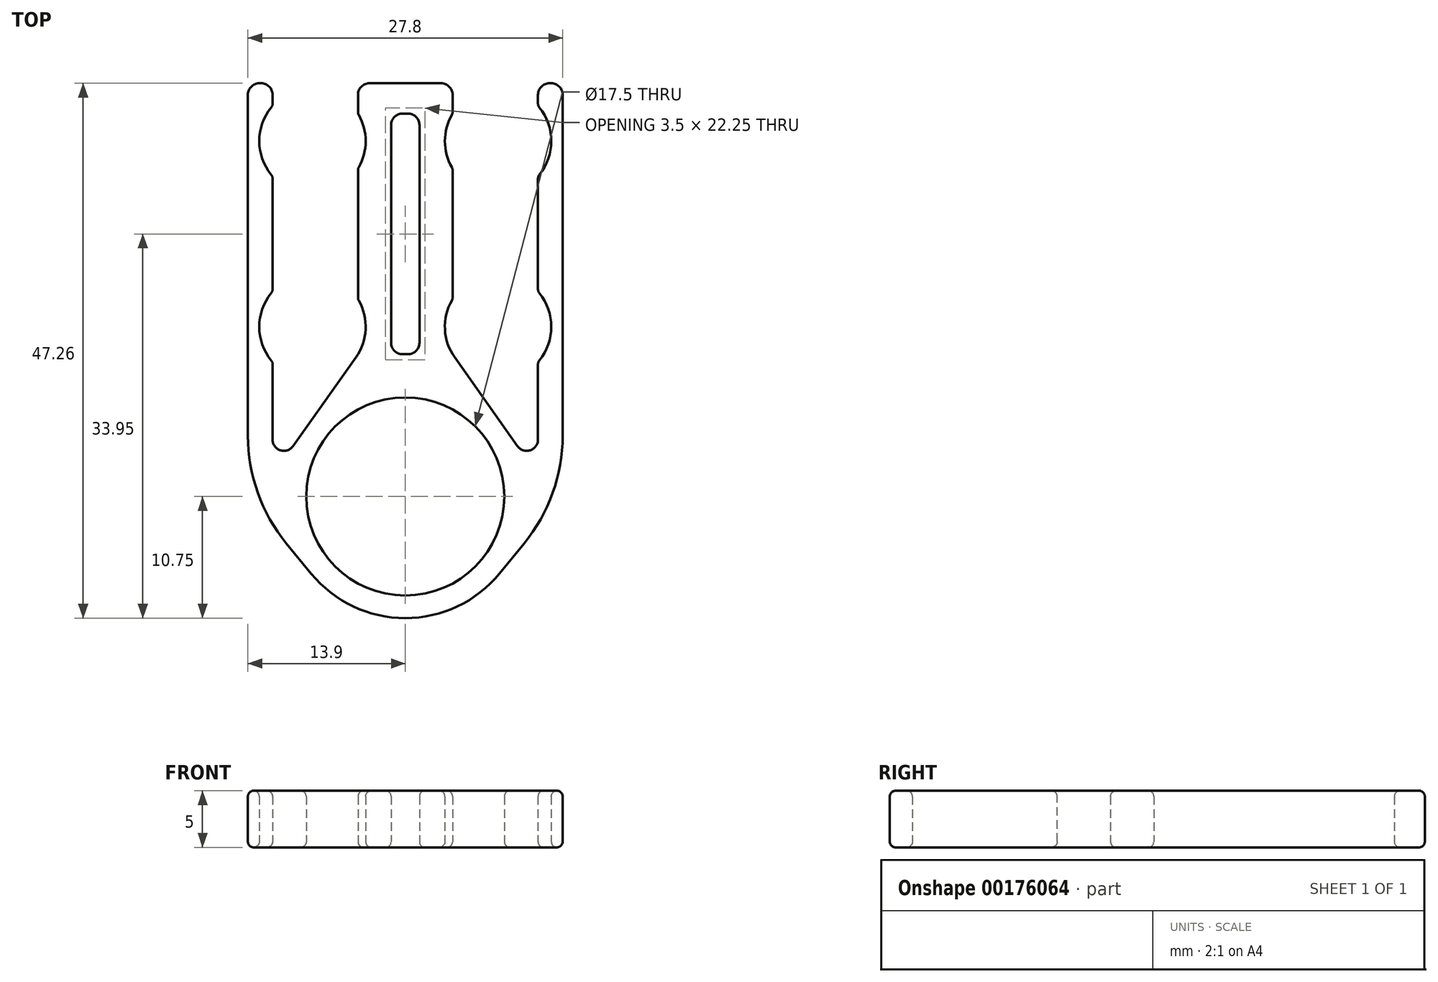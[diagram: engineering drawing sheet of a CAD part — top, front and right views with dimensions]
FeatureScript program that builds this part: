
annotation { "Feature Type Name" : "Feature", "Feature Type Description" : "" }
export const myFeature = defineFeature(function(context is Context, id is Id, definition is map)
    precondition{}
    {
        {
            var Q0;
            Q0=qCreatedBy(makeId("Top.planeOp"),FACE);
            var sketch = newSketch(context, id + "F0", { "sketchPlane" : qUnion([Q0])});
            skArc(sketch, "E0", {"start": v(-3.53, 3.1) * mm, "mid": v(-4.7, 0) * mm, "end": v(-3.53, -3.1) * mm});
            skArc(sketch, "E1.0.1.0", {"start": v(-3.53, 19.5) * mm, "mid": v(-4.7, 16.4) * mm, "end": v(-3.53, 13.3) * mm});
            skArc(sketch, "E1.1.0.0", {"start": v(19.92, -3.1) * mm, "mid": v(21.1, 0) * mm, "end": v(19.92, 3.1) * mm});
            skArc(sketch, "E1.1.1.0", {"start": v(19.92, 13.3) * mm, "mid": v(21.1, 16.4) * mm, "end": v(19.92, 19.5) * mm});
            skLineSegment(sketch, "E1.direction1", {"start": v(0, 0) * mm, "end": v(16.4, 0) * mm, "construction": true});
            skLineSegment(sketch, "E1.direction2", {"start": v(0, 0) * mm, "end": v(0, 16.4) * mm, "construction": true});
            skLineSegment(sketch, "E2", {"start": v(0, 16.4) * mm, "end": v(-4.7, 16.4) * mm, "construction": true});
            skLineSegment(sketch, "E3", {"start": v(16.4, 16.4) * mm, "end": v(21.1, 16.4) * mm, "construction": true});
            skLineSegment(sketch, "E4", {"start": v(16.4, 16.4) * mm, "end": v(11.7, 16.4) * mm, "construction": true});
            skLineSegment(sketch, "E5", {"start": v(0, 16.4) * mm, "end": v(4.7, 16.4) * mm, "construction": true});
            skPoint(sketch, "E6.startSnap0", {"position": v(-2.35, 16.4) * mm});
            skLineSegment(sketch, "E7", {"start": v(8.2, 0) * mm, "end": v(8.2, 16.4) * mm, "construction": true});
            skLineSegment(sketch, "E8", {"start": v(-4.7, 16.4) * mm, "end": v(-2.35, 16.4) * mm, "construction": true});
            skLineSegment(sketch, "E9", {"start": v(-3.53, 13.3) * mm, "end": v(-3.53, 3.1) * mm});
            skPoint(sketch, "E9.startSnap0", {"position": v(-3.53, 16.4) * mm});
            skLineSegment(sketch, "E10.MirrorCS", {"start": v(3.53, 13.3) * mm, "end": v(3.53, 3.1) * mm, "construction": true});
            skLineSegment(sketch, "E11.MirrorCS", {"start": v(19.92, 13.3) * mm, "end": v(19.92, 3.1) * mm});
            skLineSegment(sketch, "E12", {"start": v(-5.7, 21.5) * mm, "end": v(-5.7, 0) * mm});
            skLineSegment(sketch, "E13.0", {"start": v(4.03, 13.97) * mm, "end": v(4.03, 2.43) * mm});
            skLineSegment(sketch, "E14.MirrorCS", {"start": v(12.37, 13.97) * mm, "end": v(12.37, 2.43) * mm});
            skLineSegment(sketch, "E15", {"start": v(-5.7, 0) * mm, "end": v(-5.7, -15) * mm});
            skLineSegment(sketch, "E16", {"start": v(-3.53, -3.1) * mm, "end": v(-3.53, -13.1) * mm});
            skLineSegment(sketch, "E17", {"start": v(-3.53, -13.1) * mm, "end": v(3.84, -2.72) * mm});
            skCircle(sketch, "E18", {"center": v(8.2, -15) * mm, "radius": 8.75 * mm});
            skArc(sketch, "E19.0", {"start": v(-0.11, -21.81) * mm, "mid": v(8.2, -25.75) * mm, "end": v(16.51, -21.81) * mm});
            skLineSegment(sketch, "E20", {"start": v(-5.7, -15) * mm, "end": v(-0.11, -21.81) * mm});
            skLineSegment(sketch, "E21", {"start": v(-3.53, 19.5) * mm, "end": v(-3.53, 21.5) * mm});
            skLineSegment(sketch, "E22", {"start": v(-3.53, 21.5) * mm, "end": v(-5.7, 21.5) * mm});
            skPoint(sketch, "E23.orphan", {"position": v(-5.7, 16.4) * mm});
            skLineSegment(sketch, "E24", {"start": v(8.2, 16.4) * mm, "end": v(8.2, 21.5) * mm, "construction": true});
            skLineSegment(sketch, "E25", {"start": v(8.2, 21.5) * mm, "end": v(4.03, 21.5) * mm});
            skLineSegment(sketch, "E26", {"start": v(4.03, 21.5) * mm, "end": v(4.03, 18.83) * mm});
            skLineSegment(sketch, "E27.MirrorCS", {"start": v(8.2, 21.5) * mm, "end": v(12.37, 21.5) * mm});
            skLineSegment(sketch, "E28.MirrorCS", {"start": v(12.37, 21.5) * mm, "end": v(12.37, 18.83) * mm});
            skLineSegment(sketch, "E29.MirrorCS", {"start": v(19.92, 19.5) * mm, "end": v(19.92, 21.5) * mm});
            skLineSegment(sketch, "E30.MirrorCS", {"start": v(19.92, 21.5) * mm, "end": v(22.1, 21.5) * mm});
            skLineSegment(sketch, "E31.MirrorCS", {"start": v(22.1, 21.5) * mm, "end": v(22.1, 0) * mm});
            skLineSegment(sketch, "E32.MirrorCS", {"start": v(22.1, 0) * mm, "end": v(22.1, -15) * mm});
            skLineSegment(sketch, "E33.MirrorCS", {"start": v(22.1, -15) * mm, "end": v(16.51, -21.81) * mm});
            skLineSegment(sketch, "E34.MirrorCS", {"start": v(19.92, -13.1) * mm, "end": v(12.56, -2.72) * mm});
            skLineSegment(sketch, "E35.MirrorCS", {"start": v(19.92, -3.1) * mm, "end": v(19.92, -13.1) * mm});
            skArc(sketch, "E36.trimOffspring", {"start": v(17.7, -9.96) * mm, "mid": v(16.97, -8.79) * mm, "end": v(16.1, -7.71) * mm});
            skArc(sketch, "E37.trimOffspring", {"start": v(0.3, -7.71) * mm, "mid": v(-0.57, -8.79) * mm, "end": v(-1.3, -9.96) * mm});
            skArc(sketch, "E38.trimOffspring", {"start": v(12.37, 2.43) * mm, "mid": v(11.7, -0.17) * mm, "end": v(12.56, -2.72) * mm});
            skArc(sketch, "E39.trimOffspring", {"start": v(12.37, 18.83) * mm, "mid": v(11.7, 16.4) * mm, "end": v(12.37, 13.97) * mm});
            skArc(sketch, "E40.trimOffspring", {"start": v(3.53, 13.3) * mm, "mid": v(4.68, 15.98) * mm, "end": v(4.03, 18.83) * mm});
            skArc(sketch, "E41.trimOffspring", {"start": v(3.84, -2.72) * mm, "mid": v(4.7, 0.25) * mm, "end": v(3.53, 3.1) * mm});
            skLineSegment(sketch, "E42.bottom", {"start": v(9.45, 18.83) * mm, "end": v(6.95, 18.83) * mm});
            skLineSegment(sketch, "E42.top", {"start": v(9.45, -2.43) * mm, "end": v(6.95, -2.43) * mm});
            skLineSegment(sketch, "E42.left", {"start": v(9.45, 18.83) * mm, "end": v(9.45, -2.43) * mm});
            skLineSegment(sketch, "E42.right", {"start": v(6.95, 18.83) * mm, "end": v(6.95, -2.43) * mm});
            skPoint(sketch, "E42.middle", {"position": v(8.2, 8.2) * mm});
            skSolve(sketch);
        }
        {
            var Q0;
            Q0=makeQuery(id+"F0.imprint","IMPRINT",FACE,{"disambiguationData":[TD([[makeQuery(id+"F0.imprint","IMPRINT",EDGE,{"derivedFrom":sQuery(id+"F0.wireOp",EDGE,"E0")}),-1.0]])]});
            extrude(context, id + "F1", {"entities" : qUnion([Q0]), "depth" : 5 * mm});
        }
        {
            var Q0;
            Q0=makeQuery(id+"F1.opExtrude","SWEPT_EDGE",EDGE,{"disambiguationData":[OSD([sQuery(id+"F0.wireOp",EDGE,"E16"),sQuery(id+"F0.wireOp",EDGE,"E17")])]});
            var Q1;
            Q1=makeQuery(id+"F1.opExtrude","SWEPT_EDGE",EDGE,{"disambiguationData":[OSD([sQuery(id+"F0.wireOp",EDGE,"E34.MirrorCS"),sQuery(id+"F0.wireOp",EDGE,"E35.MirrorCS")])]});
            var Q2;
            Q2=makeQuery(id+"F1.opExtrude","SWEPT_EDGE",EDGE,{"disambiguationData":[OSD([sQuery(id+"F0.wireOp",EDGE,"E25"),sQuery(id+"F0.wireOp",EDGE,"E26")])]});
            var Q3;
            Q3=makeQuery(id+"F1.opExtrude","SWEPT_EDGE",EDGE,{"disambiguationData":[OSD([sQuery(id+"F0.wireOp",EDGE,"E12"),sQuery(id+"F0.wireOp",EDGE,"E22")])]});
            var Q4;
            Q4=makeQuery(id+"F1.opExtrude","SWEPT_EDGE",EDGE,{"disambiguationData":[OSD([sQuery(id+"F0.wireOp",EDGE,"E21"),sQuery(id+"F0.wireOp",EDGE,"E22")])]});
            var Q5;
            Q5=makeQuery(id+"F1.opExtrude","SWEPT_EDGE",EDGE,{"disambiguationData":[OSD([sQuery(id+"F0.wireOp",EDGE,"E27.MirrorCS"),sQuery(id+"F0.wireOp",EDGE,"E28.MirrorCS")])]});
            var Q6;
            Q6=makeQuery(id+"F1.opExtrude","SWEPT_EDGE",EDGE,{"disambiguationData":[OSD([sQuery(id+"F0.wireOp",EDGE,"E29.MirrorCS"),sQuery(id+"F0.wireOp",EDGE,"E30.MirrorCS")])]});
            var Q7;
            Q7=makeQuery(id+"F1.opExtrude","SWEPT_EDGE",EDGE,{"disambiguationData":[OSD([sQuery(id+"F0.wireOp",EDGE,"E30.MirrorCS"),sQuery(id+"F0.wireOp",EDGE,"E31.MirrorCS")])]});
            var Q8;
            Q8=makeQuery(id+"F1.opExtrude","SWEPT_EDGE",EDGE,{"disambiguationData":[OSD([sQuery(id+"F0.wireOp",EDGE,"E42.top"),sQuery(id+"F0.wireOp",EDGE,"E42.right")])]});
            var Q9;
            Q9=makeQuery(id+"F1.opExtrude","SWEPT_EDGE",EDGE,{"disambiguationData":[OSD([sQuery(id+"F0.wireOp",EDGE,"E42.top"),sQuery(id+"F0.wireOp",EDGE,"E42.left")])]});
            var Q10;
            Q10=makeQuery(id+"F1.opExtrude","SWEPT_EDGE",EDGE,{"disambiguationData":[OSD([sQuery(id+"F0.wireOp",EDGE,"E42.bottom"),sQuery(id+"F0.wireOp",EDGE,"E42.left")])]});
            var Q11;
            Q11=makeQuery(id+"F1.opExtrude","SWEPT_EDGE",EDGE,{"disambiguationData":[OSD([sQuery(id+"F0.wireOp",EDGE,"E42.bottom"),sQuery(id+"F0.wireOp",EDGE,"E42.right")])]});
            fillet(context, id + "F2", {"entities" : qUnion([Q0, Q1, Q2, Q3, Q4, Q5, Q6, Q7, Q8, Q9, Q10, Q11]), "radius" : 1 * mm, "tangentPropagation" : true, "allowEdgeOverflow" : false});
        }
        {
            var Q0;
            Q0=makeQuery(id+"F1.opExtrude","CAP_FACE",FACE,{"disambiguationData":[OSD([sQuery(id+"F0.wireOp",EDGE,"E0"),sQuery(id+"F0.wireOp",EDGE,"E1.0.1.0"),sQuery(id+"F0.wireOp",EDGE,"E1.1.0.0"),sQuery(id+"F0.wireOp",EDGE,"E1.1.1.0"),sQuery(id+"F0.wireOp",EDGE,"E9"),sQuery(id+"F0.wireOp",EDGE,"E11.MirrorCS"),sQuery(id+"F0.wireOp",EDGE,"E12"),sQuery(id+"F0.wireOp",EDGE,"E13.0"),sQuery(id+"F0.wireOp",EDGE,"E14.MirrorCS"),sQuery(id+"F0.wireOp",EDGE,"E15"),sQuery(id+"F0.wireOp",EDGE,"E16"),sQuery(id+"F0.wireOp",EDGE,"E17"),sQuery(id+"F0.wireOp",EDGE,"E18"),sQuery(id+"F0.wireOp",EDGE,"E19.0"),sQuery(id+"F0.wireOp",EDGE,"E20"),sQuery(id+"F0.wireOp",EDGE,"E21"),sQuery(id+"F0.wireOp",EDGE,"E22"),sQuery(id+"F0.wireOp",EDGE,"E25"),sQuery(id+"F0.wireOp",EDGE,"E26"),sQuery(id+"F0.wireOp",EDGE,"E27.MirrorCS"),sQuery(id+"F0.wireOp",EDGE,"E28.MirrorCS"),sQuery(id+"F0.wireOp",EDGE,"E29.MirrorCS"),sQuery(id+"F0.wireOp",EDGE,"E30.MirrorCS"),sQuery(id+"F0.wireOp",EDGE,"E31.MirrorCS"),sQuery(id+"F0.wireOp",EDGE,"E32.MirrorCS"),sQuery(id+"F0.wireOp",EDGE,"E33.MirrorCS"),sQuery(id+"F0.wireOp",EDGE,"E34.MirrorCS"),sQuery(id+"F0.wireOp",EDGE,"E35.MirrorCS"),sQuery(id+"F0.wireOp",EDGE,"E38.trimOffspring"),sQuery(id+"F0.wireOp",EDGE,"E39.trimOffspring"),sQuery(id+"F0.wireOp",EDGE,"E40.trimOffspring"),sQuery(id+"F0.wireOp",EDGE,"E41.trimOffspring")])],"isStart":false});
            var Q1;
            Q1=makeQuery(id+"F1.opExtrude","CAP_FACE",FACE,{"disambiguationData":[OSD([sQuery(id+"F0.wireOp",EDGE,"E0"),sQuery(id+"F0.wireOp",EDGE,"E1.0.1.0"),sQuery(id+"F0.wireOp",EDGE,"E1.1.0.0"),sQuery(id+"F0.wireOp",EDGE,"E1.1.1.0"),sQuery(id+"F0.wireOp",EDGE,"E9"),sQuery(id+"F0.wireOp",EDGE,"E11.MirrorCS"),sQuery(id+"F0.wireOp",EDGE,"E12"),sQuery(id+"F0.wireOp",EDGE,"E13.0"),sQuery(id+"F0.wireOp",EDGE,"E14.MirrorCS"),sQuery(id+"F0.wireOp",EDGE,"E15"),sQuery(id+"F0.wireOp",EDGE,"E16"),sQuery(id+"F0.wireOp",EDGE,"E17"),sQuery(id+"F0.wireOp",EDGE,"E18"),sQuery(id+"F0.wireOp",EDGE,"E19.0"),sQuery(id+"F0.wireOp",EDGE,"E20"),sQuery(id+"F0.wireOp",EDGE,"E21"),sQuery(id+"F0.wireOp",EDGE,"E22"),sQuery(id+"F0.wireOp",EDGE,"E25"),sQuery(id+"F0.wireOp",EDGE,"E26"),sQuery(id+"F0.wireOp",EDGE,"E27.MirrorCS"),sQuery(id+"F0.wireOp",EDGE,"E28.MirrorCS"),sQuery(id+"F0.wireOp",EDGE,"E29.MirrorCS"),sQuery(id+"F0.wireOp",EDGE,"E30.MirrorCS"),sQuery(id+"F0.wireOp",EDGE,"E31.MirrorCS"),sQuery(id+"F0.wireOp",EDGE,"E32.MirrorCS"),sQuery(id+"F0.wireOp",EDGE,"E33.MirrorCS"),sQuery(id+"F0.wireOp",EDGE,"E34.MirrorCS"),sQuery(id+"F0.wireOp",EDGE,"E35.MirrorCS"),sQuery(id+"F0.wireOp",EDGE,"E38.trimOffspring"),sQuery(id+"F0.wireOp",EDGE,"E39.trimOffspring"),sQuery(id+"F0.wireOp",EDGE,"E40.trimOffspring"),sQuery(id+"F0.wireOp",EDGE,"E41.trimOffspring")])],"isStart":true});
            var Q2;
            Q2=makeQuery(id+"F1.opExtrude","SWEPT_EDGE",EDGE,{"disambiguationData":[OSD([sQuery(id+"F0.wireOp",EDGE,"E0"),sQuery(id+"F0.wireOp",EDGE,"E9")])]});
            var Q3;
            Q3=makeQuery(id+"F1.opExtrude","SWEPT_EDGE",EDGE,{"disambiguationData":[OSD([sQuery(id+"F0.wireOp",EDGE,"E0"),sQuery(id+"F0.wireOp",EDGE,"E16")])]});
            var Q4;
            Q4=makeQuery(id+"F1.opExtrude","SWEPT_EDGE",EDGE,{"disambiguationData":[OSD([sQuery(id+"F0.wireOp",EDGE,"E1.0.1.0"),sQuery(id+"F0.wireOp",EDGE,"E9")])]});
            var Q5;
            Q5=makeQuery(id+"F1.opExtrude","SWEPT_EDGE",EDGE,{"disambiguationData":[OSD([sQuery(id+"F0.wireOp",EDGE,"E1.0.1.0"),sQuery(id+"F0.wireOp",EDGE,"E21")])]});
            var Q6;
            Q6=makeQuery(id+"F1.opExtrude","SWEPT_EDGE",EDGE,{"disambiguationData":[OSD([sQuery(id+"F0.wireOp",EDGE,"E14.MirrorCS"),sQuery(id+"F0.wireOp",EDGE,"E39.trimOffspring")])]});
            var Q7;
            Q7=makeQuery(id+"F1.opExtrude","SWEPT_EDGE",EDGE,{"disambiguationData":[OSD([sQuery(id+"F0.wireOp",EDGE,"E28.MirrorCS"),sQuery(id+"F0.wireOp",EDGE,"E39.trimOffspring")])]});
            var Q8;
            Q8=makeQuery(id+"F1.opExtrude","SWEPT_EDGE",EDGE,{"disambiguationData":[OSD([sQuery(id+"F0.wireOp",EDGE,"E14.MirrorCS"),sQuery(id+"F0.wireOp",EDGE,"E38.trimOffspring")])]});
            var Q9;
            Q9=makeQuery(id+"F1.opExtrude","SWEPT_EDGE",EDGE,{"disambiguationData":[OSD([sQuery(id+"F0.wireOp",EDGE,"E13.0"),sQuery(id+"F0.wireOp",EDGE,"E41.trimOffspring")])]});
            var Q10;
            Q10=makeQuery(id+"F1.opExtrude","SWEPT_EDGE",EDGE,{"disambiguationData":[OSD([sQuery(id+"F0.wireOp",EDGE,"E13.0"),sQuery(id+"F0.wireOp",EDGE,"E40.trimOffspring")])]});
            var Q11;
            Q11=makeQuery(id+"F1.opExtrude","SWEPT_EDGE",EDGE,{"disambiguationData":[OSD([sQuery(id+"F0.wireOp",EDGE,"E26"),sQuery(id+"F0.wireOp",EDGE,"E40.trimOffspring")])]});
            var Q12;
            Q12=makeQuery(id+"F1.opExtrude","SWEPT_EDGE",EDGE,{"disambiguationData":[OSD([sQuery(id+"F0.wireOp",EDGE,"E1.1.1.0"),sQuery(id+"F0.wireOp",EDGE,"E29.MirrorCS")])]});
            var Q13;
            Q13=makeQuery(id+"F1.opExtrude","SWEPT_EDGE",EDGE,{"disambiguationData":[OSD([sQuery(id+"F0.wireOp",EDGE,"E1.1.1.0"),sQuery(id+"F0.wireOp",EDGE,"E11.MirrorCS")])]});
            var Q14;
            Q14=makeQuery(id+"F1.opExtrude","SWEPT_EDGE",EDGE,{"disambiguationData":[OSD([sQuery(id+"F0.wireOp",EDGE,"E1.1.0.0"),sQuery(id+"F0.wireOp",EDGE,"E35.MirrorCS")])]});
            var Q15;
            Q15=makeQuery(id+"F1.opExtrude","SWEPT_EDGE",EDGE,{"disambiguationData":[OSD([sQuery(id+"F0.wireOp",EDGE,"E1.1.0.0"),sQuery(id+"F0.wireOp",EDGE,"E11.MirrorCS")])]});
            fillet(context, id + "F3", {"entities" : qUnion([Q0, Q1, Q2, Q3, Q4, Q5, Q6, Q7, Q8, Q9, Q10, Q11, Q12, Q13, Q14, Q15]), "radius" : 0.5 * mm, "tangentPropagation" : true, "allowEdgeOverflow" : false});
        }
        {
            var Q0;
            Q0=makeQuery(id+"F1.opExtrude","SWEPT_EDGE",EDGE,{"disambiguationData":[OSD([sQuery(id+"F0.wireOp",EDGE,"E32.MirrorCS"),sQuery(id+"F0.wireOp",EDGE,"E33.MirrorCS")])]});
            var Q1;
            Q1=makeQuery(id+"F1.opExtrude","SWEPT_EDGE",EDGE,{"disambiguationData":[OSD([sQuery(id+"F0.wireOp",EDGE,"E15"),sQuery(id+"F0.wireOp",EDGE,"E20")])]});
            fillet(context, id + "F4", {"entities" : qUnion([Q0, Q1]), "radius" : 15 * mm, "tangentPropagation" : true, "allowEdgeOverflow" : false});
        }
    });
